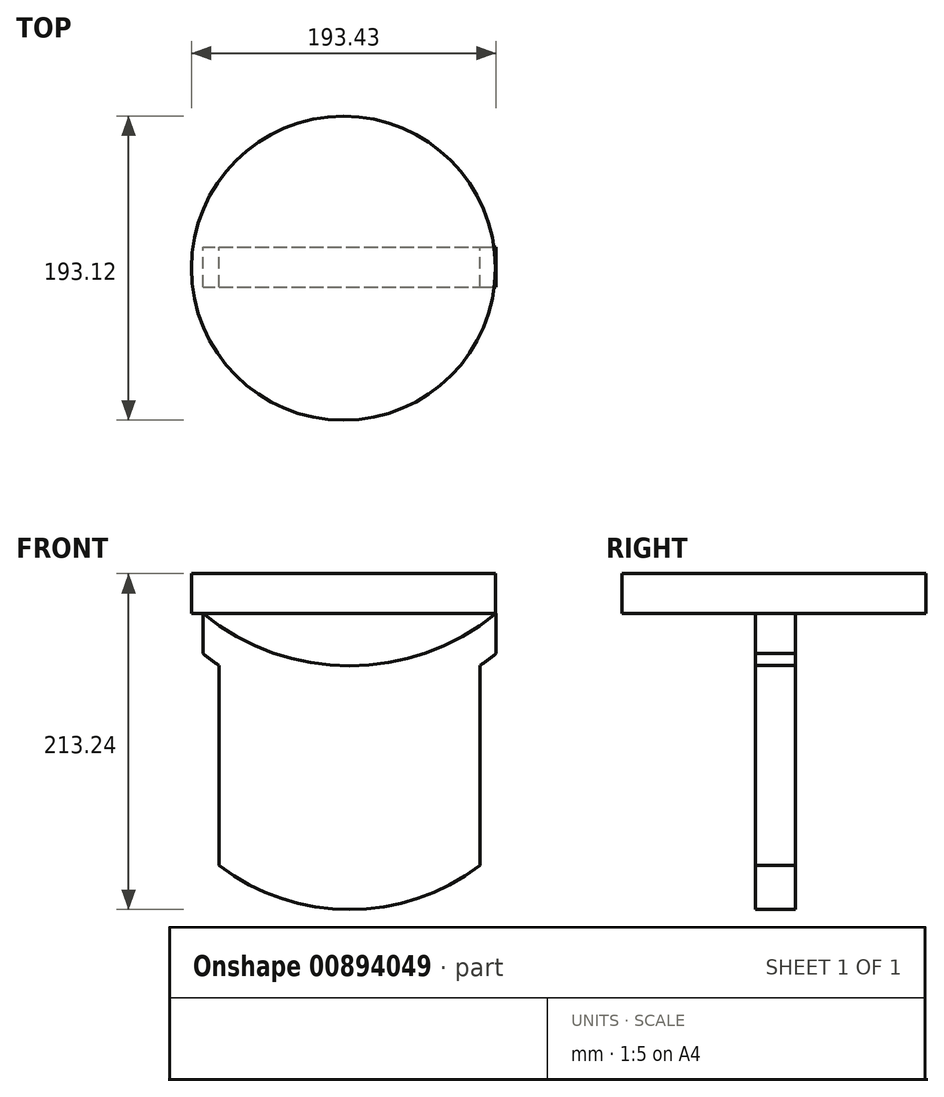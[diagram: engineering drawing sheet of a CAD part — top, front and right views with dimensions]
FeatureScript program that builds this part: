
annotation { "Feature Type Name" : "Feature", "Feature Type Description" : "" }
export const myFeature = defineFeature(function(context is Context, id is Id, definition is map)
    precondition{}
    {
        {
            var Q0;
            Q0=qCreatedBy(makeId("Front.planeOp"),FACE);
            var sketch = newSketch(context, id + "F0", { "sketchPlane" : qUnion([Q0])});
            skArc(sketch, "E0", {"start": v(-89.2, 0) * mm, "mid": v(3.84, -33.1) * mm, "end": v(96.87, 0) * mm});
            skLineSegment(sketch, "E1", {"start": v(-89.2, -25.4) * mm, "end": v(-89.2, 0) * mm});
            skLineSegment(sketch, "E2", {"start": v(96.87, 0) * mm, "end": v(96.87, -25.4) * mm});
            skArc(sketch, "E3", {"start": v(-89.2, -25.4) * mm, "mid": v(3.84, -58.5) * mm, "end": v(96.87, -25.4) * mm});
            skLineSegment(sketch, "E4", {"start": v(-79.01, -32.99) * mm, "end": v(-79.01, -159.99) * mm});
            skLineSegment(sketch, "E5", {"start": v(86.7, -32.99) * mm, "end": v(86.7, -159.99) * mm});
            skArc(sketch, "E6", {"start": v(-79.01, -159.99) * mm, "mid": v(3.84, -187.84) * mm, "end": v(86.7, -159.99) * mm});
            skSolve(sketch);
        }
        {
            var Q0;
            Q0 = qSketchRegion(id + "F0", true);
            extrude(context, id + "F1", {"entities" : qUnion([Q0]), "depth" : 25.4 * mm, "offsetDistance" : 25.4 * mm});
        }
        {
            var Q0;
            Q0=qCreatedBy(makeId("Top.planeOp"),FACE);
            var sketch = newSketch(context, id + "F2", { "sketchPlane" : qUnion([Q0])});
            skCircle(sketch, "E7", {"center": v(0, -13.51) * mm, "radius": 96.56 * mm});
            skSolve(sketch);
        }
        {
            var Q0;
            Q0 = qSketchRegion(id + "F2", true);
            extrude(context, id + "F3", {"entities" : qUnion([Q0]), "depth" : 25.4 * mm, "offsetDistance" : 25.4 * mm});
        }
    });
